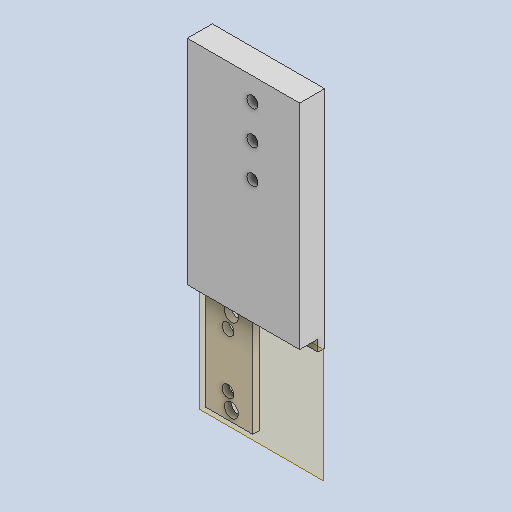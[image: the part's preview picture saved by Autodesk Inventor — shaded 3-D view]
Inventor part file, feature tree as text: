
AUTODESK INVENTOR PART (.ipt)
format: ipt  version: 2022 (Build 260153000, 153)  size: 154,624 bytes
history: native  units: in
note: dims shown in document units (in); Inventor stores cm internally (conversion verified against a paired STEP export)
features: other x5, sketch x4, extrude x2, reference x2, plane x1
ambient origin geometry x8: Origin, YZ Plane, XZ Plane, XY Plane, X Axis, Y Axis, Z Axis, Center Point
bodies: Solid1 (feature_tree)
feature tree (14):
  other  "endcap insert.ipt"
  extrude  "Extrusion1"  Depth=0.3937in
  extrude  "Extrusion2"  TaperAngle=0.0deg  [1 undecoded]
  other  "Solid1::endcap insert.ipt"
  other  "TaggingFeature1"
  sketch  "Sketch1"  dims[d0=0.3937in d1=0.0039in]
  sketch  "Sketch3"  dims[d2=0.3937in d3=0.0in d4=0.0in d5=0.0in]
  plane  "Work Plane1"
  sketch  "Sketch4"
  reference  "Reference1"
  sketch  "Sketch5"
  reference  "Reference2"
  other  "Linear Rail Assembly.iam"
  other  "Linear Rail Front Plate:1"
note: 1 required parameter value undecoded (feature->parameter linkage not recoverable at this tier; creation-order binding heuristic only, values carry confidence <= 0.55)
